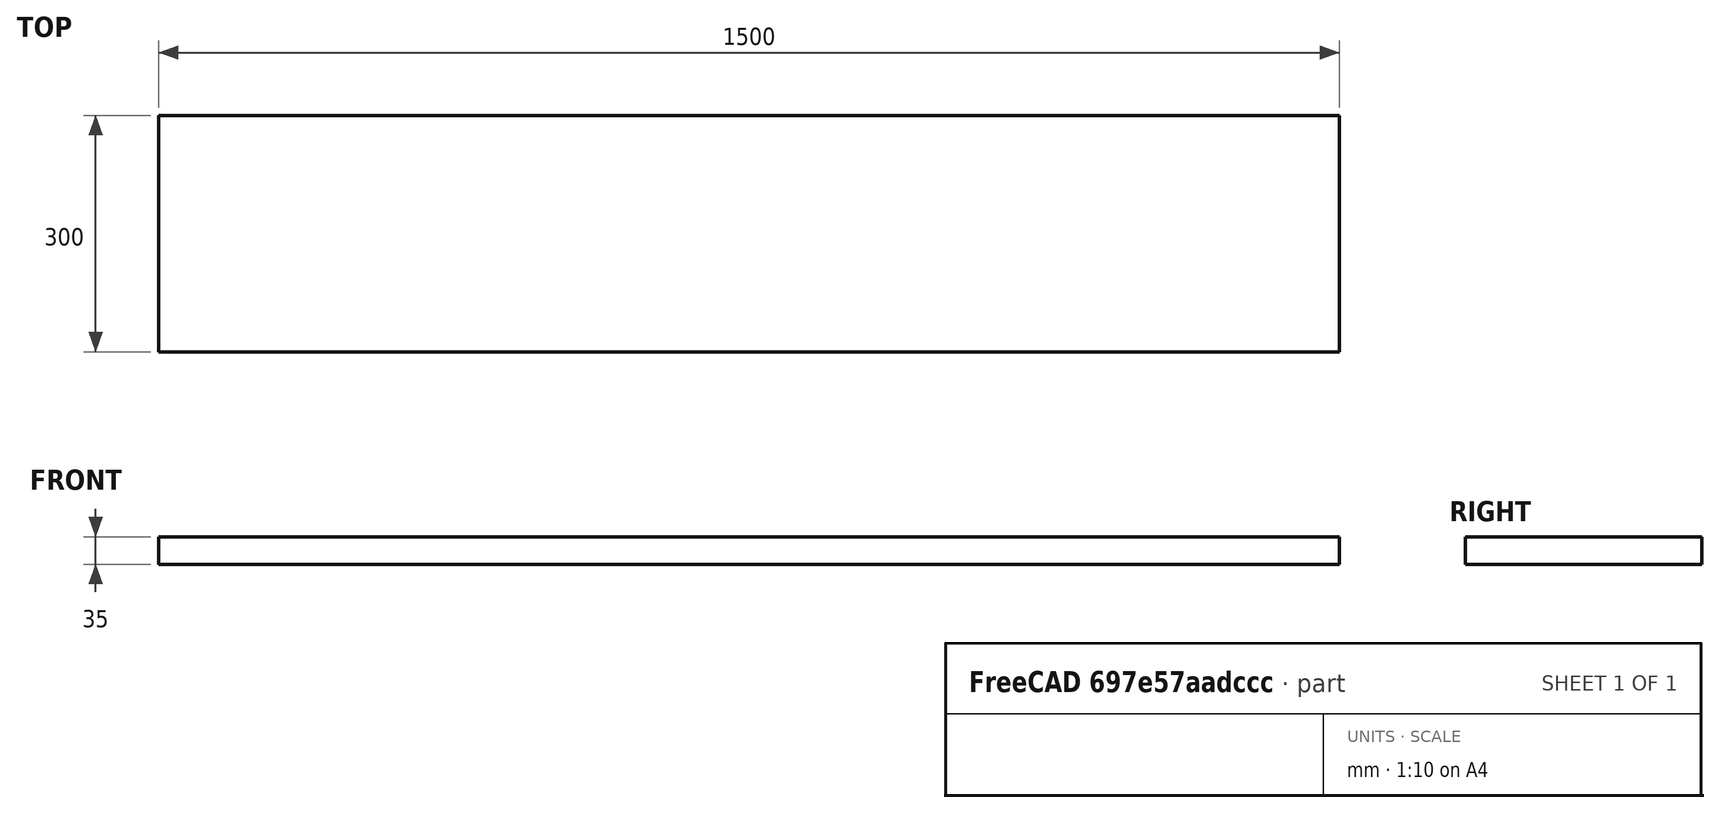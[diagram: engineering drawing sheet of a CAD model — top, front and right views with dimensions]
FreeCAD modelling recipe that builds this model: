
FCSTD DOCUMENT  (FreeCAD 0.18R4 (GitTag))
Label: benchtop_exterior
License: All rights reserved
LicenseURL: http://en.wikipedia.org/wiki/All_rights_reserved
objects: Sketcher::SketchObject×1, PartDesign::Pad×1, PartDesign::Body×1
note: 4 computed .brp shape members not serialized (recipe doc carries the construction recipe); baked Part::Feature solids carry a one-line shape summary decoded from their .brp

FEATURE [Sketcher::SketchObject] Sketch
  MapMode = 5
  Placement = pos=(0,0,0) rot=(0.57735,0.57735,0.57735;2.0944rad)
  Support = -> [YZ_Plane]
  sketch-geometry (4):
    g0: LineSegment StartX=0 StartY=0 StartZ=0 EndX=-300 EndY=0 EndZ=0
    g1: LineSegment StartX=-300 StartY=0 StartZ=0 EndX=-300 EndY=35 EndZ=0
    g2: LineSegment StartX=-300 StartY=35 StartZ=0 EndX=0 EndY=35 EndZ=0
    g3: LineSegment StartX=0 StartY=35 StartZ=0 EndX=0 EndY=0 EndZ=0
  constraints (11):
    c: Coincident(g0,g1)
    c: Coincident(g1,g2)
    c: Coincident(g2,g3)
    c: Coincident(g3,g0)
    c: Horizontal(g0)
    c: Horizontal(g2)
    c: Vertical(g1)
    c: Vertical(g3)
    c: Coincident(g0,g-1)
    c: DistanceY(g3,g3) = 35
    c: DistanceX(g0,g0) = 300
FEATURE [PartDesign::Pad] Pad
  Length = 1500
  Length2 = 100
  Placement = pos=(0,0,0) rot=(0.57735,0.57735,0.57735;2.0944rad)
  Profile = -> Sketch
  Type = 0
FEATURE [PartDesign::Body] Body
  Group = -> [Sketch,Pad]
  Origin = -> Origin
  Tip = -> Pad
